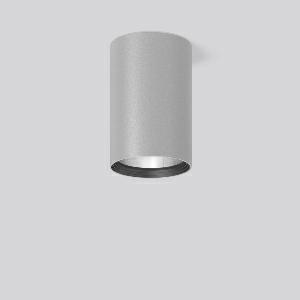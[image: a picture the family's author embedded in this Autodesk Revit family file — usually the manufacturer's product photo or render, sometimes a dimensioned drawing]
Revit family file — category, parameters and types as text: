
# Revit family: heledon_maxi_a_931225_004_76_d8d3
name_source: partatom
category: Lighting Fixtures
units: mm (PartAtom-declared; Revit-internal decimal feet)

## family parameters
Cut with Voids When Loaded = No
Host = Face
Light Source = No
Part Type = Normal
Room Calculation Point = No
Round Connector Dimension = Use Diameter
Shared = No

## types (1)
- HELEDON maxi A (1 x LED Modul 930, 4350 lm, 3000)
    Apparent Load = 35 VA
    Approval mark = CE
    CIE Flux Codes = 100 100 100 100 100
    Color Rendering = 90
    Color Temperature = 3000
    Default Elevation = 1800 mm
    Description = Series: HELEDON maxi
Cylindrical surface-mounted downlight. Housing: die-cast aluminium, powder-coated. Internal ceiling frame polycarbonate with bayonet mounting. Black plastic ring and recessed LED to prevent glare from the side. Optical assembly with reflector made of MIRO-Silver with 98% total light reflection for outstanding efficiency - can be changed without tools. Best colour rendering index Ra>90. Suitable for Ceiling mounting. Easy installation with a separate ceiling frame with bayonet mounting and plug connection. Driver integrated. Connected via plug-in connector. High quality converter without flickering and stroboscopic effect. The following accessories can be mounted without use of tools: interchangeable lenses, decorative glasses, honeycomb louvre, clear and frosted diffusers, white interchangeable plastic ring. 
Colour: silver
Diameter: 123 mm
Height: 183 mm
Lamp: LED
Socket: without socket
Colour temperature: 3000K
Colour rendering index (CRI): 92
System power: 35 W
Rated luminous flux: 4350 lm
Luminous efficiency: 124 lm/W
Control gear: Converter, dimmable, DALI
Protection class: I
Type of protection: IP 20
    Height = 183 mm
    Lamp = 1 x LED Modul 930
    Lamp Light Flux = 4350 lm
    Lamp count = 1
    Length = 123 mm
    Lifetime = 50000 h
    Luminous efficacy = 124 lm/W
    Manufacturer = RZB
    ModVariant = No
    Model = 931225.004.76
    Mounting Place = Ceiling
    Mounting Type = Surface mounted
    Number of Poles = 1
    OnlyDefault = Yes
    Power Factor = 1
    Product Name = HELEDON maxi A
    Product group = Surface mounted downlights
    ProductGroupID = 302
    Protection Class = Protection class I
    Protection Degree = IP 20
    RLX_Detail_Level = 1
    RLX_Emergency_Light_Flux = 0 lm
    RLX_Emergency_Type = 0
    RLX_Emergency_Type_DB = No
    RlxData = <blob elided: 99417 chars, md5=411a03d4>
    Socket = socket
    Standby Power = 0 W
    System Light Flux = 4350 lm
    System Power = 35 W
    Type Comments = Product without accessories
    Type Image = 931192.004.jpg
    URL = http://relux.com
    VarID = ---
    Voltage = 230 V
    Voltage Range = 220-240 V
    Weight = 0.00 kg
    Width = 0 mm  [stored 0 ft]

note: [stored X ft] marks values corroborated as IEEE doubles in the binary element streams (Revit-internal decimal feet)

## geometry (parser evidence)
native form markers: Blend x4, Sweep x11
no freeform markers — native parametric forms only
